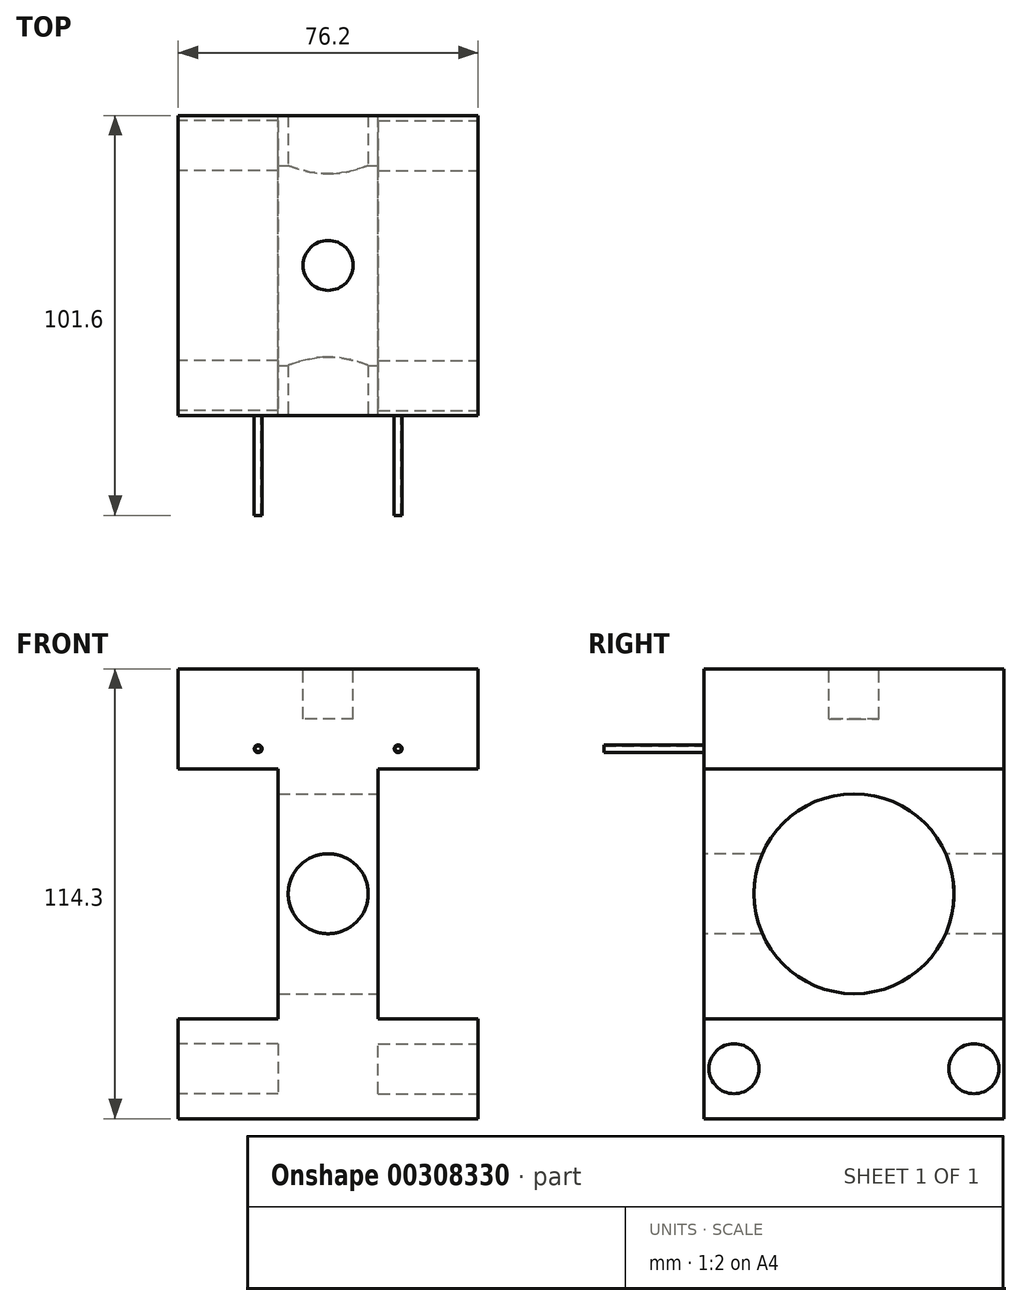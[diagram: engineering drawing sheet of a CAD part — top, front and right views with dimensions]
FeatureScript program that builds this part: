
annotation { "Feature Type Name" : "Feature", "Feature Type Description" : "" }
export const myFeature = defineFeature(function(context is Context, id is Id, definition is map)
    precondition{}
    {
        {
            var Q0;
            Q0=qCreatedBy(makeId("Front.planeOp"),FACE);
            var sketch = newSketch(context, id + "F0", { "sketchPlane" : qUnion([Q0])});
            skLineSegment(sketch, "E0", {"start": v(-44.45, -34.36) * mm, "end": v(31.75, -34.36) * mm});
            skLineSegment(sketch, "E1", {"start": v(31.75, -34.36) * mm, "end": v(31.75, -8.96) * mm});
            skLineSegment(sketch, "E2", {"start": v(31.75, -8.96) * mm, "end": v(6.35, -8.96) * mm});
            skLineSegment(sketch, "E3", {"start": v(6.35, -8.96) * mm, "end": v(6.35, 54.54) * mm});
            skLineSegment(sketch, "E4", {"start": v(6.35, 54.54) * mm, "end": v(31.75, 54.54) * mm});
            skLineSegment(sketch, "E5", {"start": v(31.75, 54.54) * mm, "end": v(31.75, 79.94) * mm});
            skLineSegment(sketch, "E6", {"start": v(31.75, 79.94) * mm, "end": v(-44.45, 79.94) * mm});
            skLineSegment(sketch, "E7", {"start": v(-44.45, 79.94) * mm, "end": v(-44.45, 54.54) * mm});
            skLineSegment(sketch, "E8", {"start": v(-44.45, 54.54) * mm, "end": v(-19.05, 54.54) * mm});
            skLineSegment(sketch, "E9", {"start": v(-19.05, 54.54) * mm, "end": v(-19.05, -8.96) * mm});
            skLineSegment(sketch, "E10", {"start": v(-19.05, -8.96) * mm, "end": v(-44.45, -8.96) * mm});
            skLineSegment(sketch, "E11", {"start": v(-44.45, -8.96) * mm, "end": v(-44.45, -34.36) * mm});
            skSolve(sketch);
        }
        {
            var Q0;
            Q0 = qSketchRegion(id + "F0", true);
            extrude(context, id + "F1", {"entities" : qUnion([Q0]), "endBound" : BoundingType.SYMMETRIC, "depth" : 76.2 * mm});
        }
        {
            var Q0;
            Q0=makeQuery(id+"F1.opExtrude","SWEPT_FACE",FACE,{"disambiguationData":[OSD([sQuery(id+"F0.wireOp",EDGE,"E3")])]});
            var sketch = newSketch(context, id + "F2", { "sketchPlane" : qUnion([Q0])});
            skCircle(sketch, "E12", {"center": v(0, 22.8) * mm, "radius": 25.4 * mm});
            skSolve(sketch);
        }
        {
            var Q0;
            Q0=sQuery(id+"F2.wireOp",VERTEX,"E12.center");
            var Q1;
            Q1=makeQuery(id+"F1.opExtrude","SWEPT_BODY",BODY,{"disambiguationData":[OSD([sQuery(id+"F0.wireOp",EDGE,"E0"),sQuery(id+"F0.wireOp",EDGE,"E1"),sQuery(id+"F0.wireOp",EDGE,"E2"),sQuery(id+"F0.wireOp",EDGE,"E3"),sQuery(id+"F0.wireOp",EDGE,"E4"),sQuery(id+"F0.wireOp",EDGE,"E5"),sQuery(id+"F0.wireOp",EDGE,"E6"),sQuery(id+"F0.wireOp",EDGE,"E7"),sQuery(id+"F0.wireOp",EDGE,"E8"),sQuery(id+"F0.wireOp",EDGE,"E9"),sQuery(id+"F0.wireOp",EDGE,"E10"),sQuery(id+"F0.wireOp",EDGE,"E11")])]});
            hole(context, id + "F3", {"style" : HoleStyle.SIMPLE, "endStyle" : HoleEndStyle.THROUGH, "holeDiameter" : 50.8 * mm, "tappedDepth" : 12.7 * mm, "tapClearance" : 3, "locations" : qUnion([Q0]), "scope" : qUnion([Q1])});
        }
        {
            var Q0;
            Q0=makeQuery(id+"F1.opExtrude","SWEPT_FACE",FACE,{"disambiguationData":[OSD([sQuery(id+"F0.wireOp",EDGE,"E11")])]});
            var sketch = newSketch(context, id + "F4", { "sketchPlane" : qUnion([Q0])});
            skCircle(sketch, "E13", {"center": v(-30.48, -21.66) * mm, "radius": 6.35 * mm});
            skPoint(sketch, "E13.centerSnap0", {"position": v(-38.1, -21.66) * mm});
            skCircle(sketch, "E14", {"center": v(30.48, -21.66) * mm, "radius": 6.35 * mm});
            skPoint(sketch, "E14.centerSnap0", {"position": v(38.1, -21.66) * mm});
            skSolve(sketch);
        }
        {
            var Q0;
            Q0=makeQuery(id+"F1.opExtrude","SWEPT_FACE",FACE,{"disambiguationData":[OSD([sQuery(id+"F0.wireOp",EDGE,"E1")])]});
            var sketch = newSketch(context, id + "F5", { "sketchPlane" : qUnion([Q0])});
            skCircle(sketch, "E15", {"center": v(-30.48, -21.66) * mm, "radius": 6.35 * mm});
            skPoint(sketch, "E15.centerSnap0", {"position": v(-38.1, -21.66) * mm});
            skCircle(sketch, "E16", {"center": v(30.48, -21.66) * mm, "radius": 6.35 * mm});
            skPoint(sketch, "E16.centerSnap0", {"position": v(38.1, -21.66) * mm});
            skSolve(sketch);
        }
        {
            var Q0;
            Q0=makeQuery(id+"F5.imprint","IMPRINT",FACE,{"disambiguationData":[TD([[makeQuery(id+"F5.imprint","IMPRINT",EDGE,{"derivedFrom":sQuery(id+"F5.wireOp",EDGE,"E15")}),1.0]])]});
            var Q1;
            Q1=makeQuery(id+"F5.imprint","IMPRINT",FACE,{"disambiguationData":[TD([[makeQuery(id+"F5.imprint","IMPRINT",EDGE,{"derivedFrom":sQuery(id+"F5.wireOp",EDGE,"E16")}),1.0]])]});
            extrude(context, id + "F6", {"entities" : qUnion([Q0, Q1]), "operationType" : NewBodyOperationType.REMOVE, "oppositeDirection" : true, "depth" : 25.4 * mm});
        }
        {
            var Q0;
            Q0=makeQuery(id+"F4.imprint","IMPRINT",FACE,{"disambiguationData":[TD([[makeQuery(id+"F4.imprint","IMPRINT",EDGE,{"derivedFrom":sQuery(id+"F4.wireOp",EDGE,"E14")}),1.0]])]});
            var Q1;
            Q1=makeQuery(id+"F4.imprint","IMPRINT",FACE,{"disambiguationData":[TD([[makeQuery(id+"F4.imprint","IMPRINT",EDGE,{"derivedFrom":sQuery(id+"F4.wireOp",EDGE,"E13")}),1.0]])]});
            extrude(context, id + "F7", {"entities" : qUnion([Q0, Q1]), "operationType" : NewBodyOperationType.REMOVE, "oppositeDirection" : true, "depth" : 25.4 * mm});
        }
        {
            var Q0;
            Q0=makeQuery(id+"F1.opExtrude","SWEPT_FACE",FACE,{"disambiguationData":[OSD([sQuery(id+"F0.wireOp",EDGE,"E6")])]});
            var sketch = newSketch(context, id + "F8", { "sketchPlane" : qUnion([Q0])});
            skCircle(sketch, "E17", {"center": v(-6.35, 0) * mm, "radius": 6.35 * mm});
            skPoint(sketch, "E17.centerSnap0", {"position": v(-44.45, 0) * mm});
            skPoint(sketch, "E17.centerSnap1", {"position": v(-6.35, 38.1) * mm});
            skSolve(sketch);
        }
        {
            var Q0;
            Q0=makeQuery(id+"F8.imprint","IMPRINT",FACE,{"disambiguationData":[TD([[makeQuery(id+"F8.imprint","IMPRINT",EDGE,{"derivedFrom":sQuery(id+"F8.wireOp",EDGE,"E17")}),1.0]])]});
            extrude(context, id + "F9", {"entities" : qUnion([Q0]), "operationType" : NewBodyOperationType.REMOVE, "oppositeDirection" : true, "depth" : 12.7 * mm});
        }
        {
            var Q0;
            Q0=makeQuery(id+"F1.opExtrude","CAP_FACE",FACE,{"disambiguationData":[OSD([sQuery(id+"F0.wireOp",EDGE,"E0"),sQuery(id+"F0.wireOp",EDGE,"E1"),sQuery(id+"F0.wireOp",EDGE,"E2"),sQuery(id+"F0.wireOp",EDGE,"E3"),sQuery(id+"F0.wireOp",EDGE,"E4"),sQuery(id+"F0.wireOp",EDGE,"E5"),sQuery(id+"F0.wireOp",EDGE,"E6"),sQuery(id+"F0.wireOp",EDGE,"E7"),sQuery(id+"F0.wireOp",EDGE,"E8"),sQuery(id+"F0.wireOp",EDGE,"E9"),sQuery(id+"F0.wireOp",EDGE,"E10"),sQuery(id+"F0.wireOp",EDGE,"E11")])],"isStart":false});
            var sketch = newSketch(context, id + "F10", { "sketchPlane" : qUnion([Q0])});
            skCircle(sketch, "E18", {"center": v(-24.13, 59.62) * mm, "radius": 1 * mm});
            skCircle(sketch, "E19", {"center": v(11.43, 59.62) * mm, "radius": 1 * mm});
            skCircle(sketch, "E20", {"center": v(-24.13, 59.62) * mm, "radius": 0.75 * mm});
            skCircle(sketch, "E21", {"center": v(11.43, 59.62) * mm, "radius": 0.75 * mm});
            skCircle(sketch, "E22", {"center": v(-6.35, 22.8) * mm, "radius": 10.16 * mm});
            skPoint(sketch, "E22.centerSnap0", {"position": v(-6.35, 79.94) * mm});
            skPoint(sketch, "E22.centerSnap1", {"position": v(-19.05, 22.8) * mm});
            skSolve(sketch);
        }
        {
            var Q0;
            Q0=makeQuery(id+"F10.imprint","IMPRINT",FACE,{"disambiguationData":[TD([[makeQuery(id+"F10.imprint","IMPRINT",EDGE,{"derivedFrom":sQuery(id+"F10.wireOp",EDGE,"E19")}),1.0]])]});
            var Q1;
            Q1=makeQuery(id+"F10.imprint","IMPRINT",FACE,{"disambiguationData":[TD([[makeQuery(id+"F10.imprint","IMPRINT",EDGE,{"derivedFrom":sQuery(id+"F10.wireOp",EDGE,"E18")}),1.0]])]});
            extrude(context, id + "F11", {"entities" : qUnion([Q0, Q1]), "operationType" : NewBodyOperationType.ADD, "depth" : 25.4 * mm});
        }
        {
            var Q0;
            Q0=makeQuery(id+"F10.imprint","IMPRINT",FACE,{"disambiguationData":[TD([[makeQuery(id+"F10.imprint","IMPRINT",EDGE,{"derivedFrom":sQuery(id+"F10.wireOp",EDGE,"E22")}),1.0]])]});
            extrude(context, id + "F12", {"entities" : qUnion([Q0]), "operationType" : NewBodyOperationType.REMOVE, "oppositeDirection" : true, "depth" : 101.6 * mm});
        }
    });
